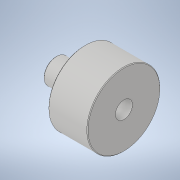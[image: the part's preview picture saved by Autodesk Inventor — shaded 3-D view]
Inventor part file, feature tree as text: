
AUTODESK INVENTOR PART (.ipt)
format: ipt  version: 2021 (Build 250183000, 183)  size: 118,272 bytes
history: native  units: in
note: dims shown in document units (in); Inventor stores cm internally (conversion verified against a paired STEP export)
features: extrude x2, sketch x2, chamfer x1
ambient origin geometry x8: Origin, YZ Plane, XZ Plane, XY Plane, X Axis, Y Axis, Z Axis, Center Point
bodies: Solid1 (feature_tree)
feature tree (5):
  extrude  "Extrusion1"  Depth=0.268in
  extrude  "Extrusion2"  Depth=0.616in
  chamfer  "Chamfer1"  Distance=0.616in
  sketch  "Sketch1"  dims[d0=0.394in d1=0.268in]
  sketch  "Sketch2"  dims[d2=0.453in d3=0.0in d4=1.15in d5=0.616in d6=0.0in d7=0.268in d9=0.01in d10=0.125in d11=45.0deg d12=0.5in d13=0.0344in d14=0.5in d15=0.0344in]
